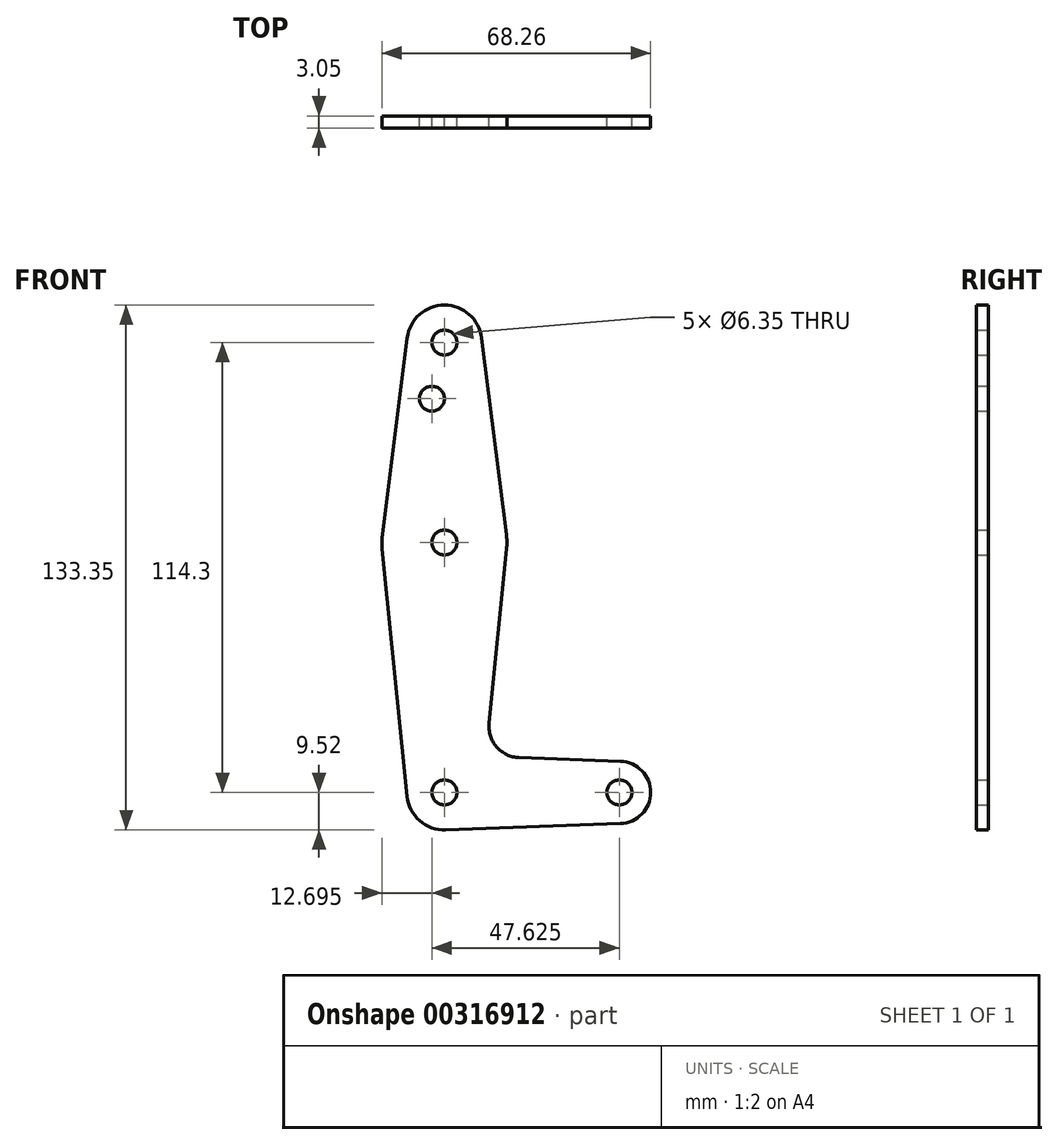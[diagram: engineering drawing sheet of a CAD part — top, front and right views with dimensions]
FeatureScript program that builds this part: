
annotation { "Feature Type Name" : "Feature", "Feature Type Description" : "" }
export const myFeature = defineFeature(function(context is Context, id is Id, definition is map)
    precondition{}
    {
        {
            var Q0;
            Q0=qCreatedBy(makeId("Front.planeOp"),FACE);
            var sketch = newSketch(context, id + "F0", { "sketchPlane" : qUnion([Q0])});
            skLineSegment(sketch, "E0", {"start": v(0, 0) * mm, "end": v(0, 114.3) * mm, "construction": true});
            skLineSegment(sketch, "E1", {"start": v(0, 0) * mm, "end": v(44.45, 0) * mm, "construction": true});
            skCircle(sketch, "E2", {"center": v(0, 114.3) * mm, "radius": 9.53 * mm});
            skCircle(sketch, "E3", {"center": v(0, 63.5) * mm, "radius": 15.88 * mm});
            skCircle(sketch, "E4", {"center": v(0, 0) * mm, "radius": 9.53 * mm});
            skCircle(sketch, "E5", {"center": v(44.45, 0) * mm, "radius": 7.94 * mm});
            skLineSegment(sketch, "E6", {"start": v(0.34, -9.52) * mm, "end": v(44.73, -7.93) * mm});
            skLineSegment(sketch, "E7", {"start": v(44.73, 7.93) * mm, "end": v(18.97, 8.85) * mm});
            skLineSegment(sketch, "E8", {"start": v(-15.8, 61.91) * mm, "end": v(-9.48, -0.95) * mm});
            skLineSegment(sketch, "E9", {"start": v(-9.45, 115.5) * mm, "end": v(-15.75, 65.48) * mm});
            skLineSegment(sketch, "E10", {"start": v(9.45, 115.5) * mm, "end": v(15.75, 65.48) * mm});
            skLineSegment(sketch, "E11", {"start": v(15.8, 61.91) * mm, "end": v(11.34, 17.6) * mm});
            skCircle(sketch, "E12", {"center": v(0, 114.3) * mm, "radius": 3.18 * mm});
            skCircle(sketch, "E13", {"center": v(-3.18, 100.03) * mm, "radius": 3.18 * mm});
            skCircle(sketch, "E14", {"center": v(0, 63.5) * mm, "radius": 3.17 * mm});
            skCircle(sketch, "E15", {"center": v(0, 0) * mm, "radius": 3.18 * mm});
            skCircle(sketch, "E16", {"center": v(44.45, 0) * mm, "radius": 3.18 * mm});
            skArc(sketch, "E17.filletArc", {"start": v(11.34, 17.6) * mm, "mid": v(13.26, 11.57) * mm, "end": v(18.97, 8.85) * mm});
            skSolve(sketch);
        }
        {
            var Q0;
            {var subQ1=sQuery(id+"F0.wireOp",EDGE,"E9");Q0=makeQuery(id+"F0.imprint","IMPRINT",FACE,{"disambiguationData":[TD([[makeQuery(id+"F0.imprint","IMPRINT",EDGE,{"derivedFrom":subQ1}),1.0]])]});}
            var Q1;
            Q1=makeQuery(id+"F0.imprint","IMPRINT",FACE,{"disambiguationData":[TD([[makeQuery(id+"F0.imprint","IMPRINT",EDGE,{"derivedFrom":sQuery(id+"F0.wireOp",EDGE,"E14")}),-1.0]])]});
            var Q2;
            {var subQ0=sQuery(id+"F0.wireOp",EDGE,"E6");Q2=makeQuery(id+"F0.imprint","IMPRINT",FACE,{"disambiguationData":[TD([[makeQuery(id+"F0.imprint","IMPRINT",EDGE,{"derivedFrom":subQ0}),1.0]])]});}
            var Q3;
            Q3=makeQuery(id+"F0.imprint","IMPRINT",FACE,{"disambiguationData":[TD([[makeQuery(id+"F0.imprint","IMPRINT",EDGE,{"derivedFrom":sQuery(id+"F0.wireOp",EDGE,"E12")}),-1.0]])]});
            var Q4;
            Q4=makeQuery(id+"F0.imprint","IMPRINT",FACE,{"disambiguationData":[TD([[makeQuery(id+"F0.imprint","IMPRINT",EDGE,{"derivedFrom":sQuery(id+"F0.wireOp",EDGE,"E16")}),-1.0]])]});
            var Q5;
            Q5=makeQuery(id+"F0.imprint","IMPRINT",FACE,{"disambiguationData":[TD([[makeQuery(id+"F0.imprint","IMPRINT",EDGE,{"derivedFrom":sQuery(id+"F0.wireOp",EDGE,"E15")}),-1.0]])]});
            extrude(context, id + "F1", {"entities" : qUnion([Q0, Q1, Q2, Q3, Q4, Q5]), "depth" : 3.05 * mm});
        }
    });
